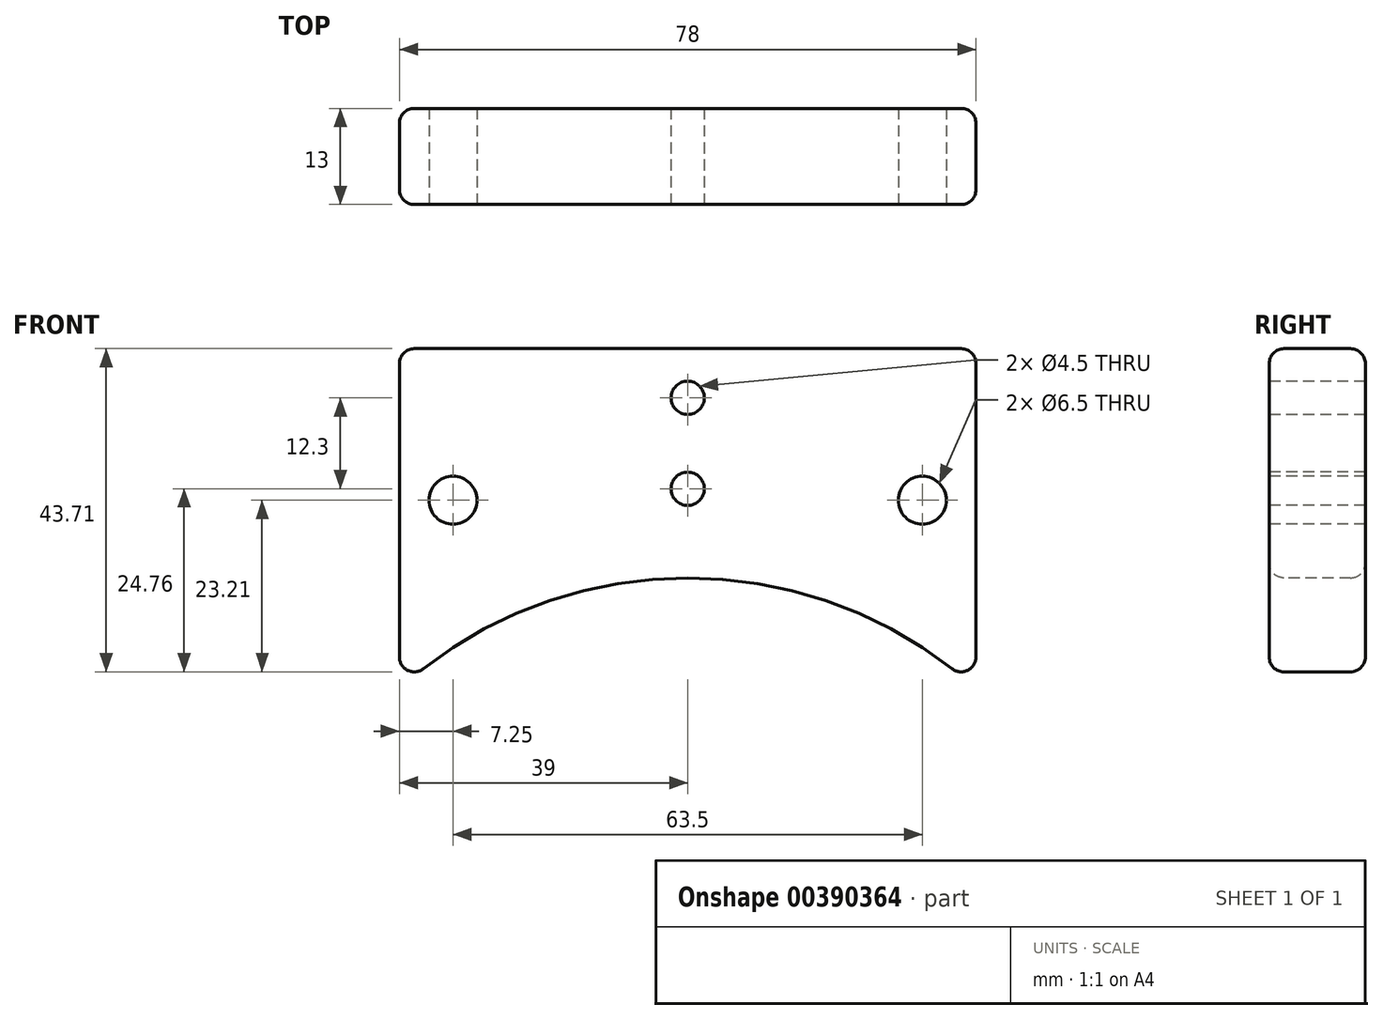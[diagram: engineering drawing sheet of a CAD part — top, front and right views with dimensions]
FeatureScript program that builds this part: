
annotation { "Feature Type Name" : "Feature", "Feature Type Description" : "" }
export const myFeature = defineFeature(function(context is Context, id is Id, definition is map)
    precondition{}
    {
        {
            var Q0;
            Q0=qCreatedBy(makeId("Front.planeOp"),FACE);
            var sketch = newSketch(context, id + "F0", { "sketchPlane" : qUnion([Q0])});
            skLineSegment(sketch, "E0", {"start": v(-39, -46) * mm, "end": v(-39, 0) * mm});
            skLineSegment(sketch, "E1", {"start": v(-39, 0) * mm, "end": v(39, 0) * mm});
            skLineSegment(sketch, "E2", {"start": v(39, 0) * mm, "end": v(39, -46) * mm});
            skArc(sketch, "E3", {"start": v(39, -46) * mm, "mid": v(0, -31) * mm, "end": v(-39, -46) * mm});
            skCircle(sketch, "E4", {"center": v(-31.75, -20.5) * mm, "radius": 3.25 * mm});
            skCircle(sketch, "E5", {"center": v(31.75, -20.5) * mm, "radius": 3.25 * mm});
            skCircle(sketch, "E6", {"center": v(0, -6.65) * mm, "radius": 2.25 * mm});
            skCircle(sketch, "E7", {"center": v(0, -18.95) * mm, "radius": 2.25 * mm});
            skSolve(sketch);
        }
        {
            var Q0;
            Q0 = qSketchRegion(id + "F0", true);
            extrude(context, id + "F1", {"entities" : qUnion([Q0]), "oppositeDirection" : true, "depth" : 13 * mm});
        }
        {
            var Q0;
            Q0=makeQuery(id+"F1.opExtrude","SWEPT_EDGE",EDGE,{"disambiguationData":[OSD([sQuery(id+"F0.wireOp",EDGE,"E0"),sQuery(id+"F0.wireOp",EDGE,"E3")])]});
            var Q1;
            Q1=makeQuery(id+"F1.opExtrude","SWEPT_EDGE",EDGE,{"disambiguationData":[OSD([sQuery(id+"F0.wireOp",EDGE,"E2"),sQuery(id+"F0.wireOp",EDGE,"E3")])]});
            fillet(context, id + "F2", {"entities" : qUnion([Q0, Q1]), "radius" : 2 * mm, "tangentPropagation" : true, "allowEdgeOverflow" : false});
        }
        {
            var Q0;
            Q0=makeQuery(id+"F1.opExtrude","SWEPT_EDGE",EDGE,{"disambiguationData":[OSD([sQuery(id+"F0.wireOp",EDGE,"E0"),sQuery(id+"F0.wireOp",EDGE,"E1")])]});
            var Q1;
            Q1=makeQuery(id+"F1.opExtrude","SWEPT_EDGE",EDGE,{"disambiguationData":[OSD([sQuery(id+"F0.wireOp",EDGE,"E1"),sQuery(id+"F0.wireOp",EDGE,"E2")])]});
            var Q2;
            Q2=makeQuery(id+"F1.opExtrude","SWEPT_FACE",FACE,{"disambiguationData":[OSD([sQuery(id+"F0.wireOp",EDGE,"E1")])]});
            var Q3;
            Q3=makeQuery(id+"F1.opExtrude","SWEPT_FACE",FACE,{"disambiguationData":[OSD([sQuery(id+"F0.wireOp",EDGE,"E0")])]});
            fillet(context, id + "F3", {"entities" : qUnion([Q0, Q1, Q2, Q3]), "radius" : 2 * mm, "tangentPropagation" : true, "allowEdgeOverflow" : false});
        }
    });
